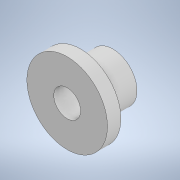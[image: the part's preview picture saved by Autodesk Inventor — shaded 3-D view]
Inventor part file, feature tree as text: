
AUTODESK INVENTOR PART (.ipt)
format: ipt  version: 2022 (Build 260153000, 153)  size: 116,736 bytes
history: native  units: in
note: dims shown in document units (in); Inventor stores cm internally (conversion verified against a paired STEP export)
features: extrude x3, sketch x3
ambient origin geometry x8: Origin, YZ Plane, XZ Plane, XY Plane, X Axis, Y Axis, Z Axis, Center Point
bodies: Solid1 (feature_tree)
feature tree (6):
  extrude  "Extrusion1"  Depth=0.1969in TaperAngle=0.0deg
  extrude  "Extrusion2"  Depth=0.6693in TaperAngle=0.0deg
  extrude  "Extrusion3"  Depth=0.6693in TaperAngle=0.0deg
  sketch  "Sketch2"  dims[d0=1.1811in d1=0.1969in d2=0.0in]
  sketch  "Sketch3"  dims[d3=0.7087in d4=0.6693in d5=0.0in]
  sketch  "Sketch4"  dims[d6=0.3937in d7=0.6693in d8=0.0in]
